# Revit family: KS Husky, Typ II-13, Ø 6 und Ø25
name_source: partatom
category: HLS-Bauteile
revit_build: Autodesk Revit 2018 (Build: 20190510_1515(x64)
units: mm (PartAtom-declared; Revit-internal decimal feet)

## family parameters
Arbeitsebenenbasiert = Ja
Beim Laden mit Abzugskörper schneiden = Nein
Bemaßung runder Anschluss = Durchmesser verwenden
Gemeinsam genutzt = Ja
Immer vertikal = Nein
Raumberechnungspunkt = Nein
Teiletyp = Normal

## types (2) — shared parameters
A = 30 mm  [stored 0.0984252 ft]
Anschlußhöhe = 30 mm
Baustoffklasse = B2
DF1 = 19 mm  [stored 0.062336 ft]
DF2 = 19 mm  [stored 0.062336 ft]
DS = 13 mm
DVS = 5 mm  [stored 0.0164042 ft]
Dichte Kern = 120 kg/m³
Dämmkörper = KA/PU
Dämmstärke = 13 mm
Fabrikat = MEFA
Firma = MEFA Befestigungs- und Montagesysteme GmbH
H1 = 2 mm  [stored 0.00656168 ft]
H2 = 3 mm  [stored 0.00984252 ft]
HGA = 16 mm  [stored 0.0524934 ft]
Kurztext1 = Kälteschelle Husky II 13
L = 36 mm  [stored 0.11811 ft]
MB = 20 mm  [stored 0.0656168 ft]
MD = 1 mm  [stored 0.00328084 ft]
Material = Stahl
Material Mantel = Kunststoff
Materialname = DD11
Mengeneinheit = St
Oberflaeche = galvanisch verzinkt
Schalenlänge = 36 mm
Typ = II 13
Vorgabe-Ansicht = 1219 mm
Wasserdampfdiffusionswiderstand = 7000 µ
Wärmeleitfähigkeit = 0.029 W/mK
max. Temperaturbeständigkeit = 105 °C
mittl. Nenndruckfestigkeit Kern = 1,35 N/mm²
stat. Belastung Kern = 0.27 N/mm²

## per-type parameters (varying)
| type | Anschluss | Artikelnummer | B | Breite | D | D0 | EAN | Gewicht | Gewicht pro Bauteil | H | Kurztext2 | R | RM | Rohraußendurchmesser Kunststoff | Rohraußendurchmesser Kupfer | Rohrschellentyp | S | max. zul. Last | vpe |
| Kälteschelle Husky, Typ II-13, M8/M10, Ø 6 | M8 | 6830060 | 71 mm  [stored 0.23294 ft] | 56 mm  [stored 0.183727 ft] | 6 mm  [stored 0.019685 ft] | 31 mm  [stored 0.101706 ft] | 4250928440341 | 0.03 kg | 0.03 kg | 49 mm  [stored 0.160761 ft] | 6 mm Iso 13 x 36 mm M8 | 16 mm  [stored 0.0524934 ft] | 17 mm  [stored 0.0557743 ft] |  | 6 mm | Sigma | 52 mm | 0.05 kN | 24 |
| Kälteschelle Husky, Typ II-13, M8/M10, Ø 25 | M8/M10 | 6830250 | 90 mm  [stored 0.295276 ft] | 88 mm  [stored 0.288714 ft] | 25 mm  [stored 0.082021 ft] | 50 mm  [stored 0.164042 ft] | 4250928440419 | 0.09 kg | 0.09 kg | 68 mm | 25 mm Iso 13 x 36 mm M8/M10 | 25 mm  [stored 0.082021 ft] | 26 mm | 25 mm | 10 mm | Trabant | 71 mm  [stored 0.23294 ft] | 0.21 kN | 12 |

note: [stored X ft] marks values corroborated as IEEE doubles in the binary element streams (Revit-internal decimal feet)

## geometry (parser evidence)
native form markers: Sweep x3
no freeform markers — native parametric forms only
